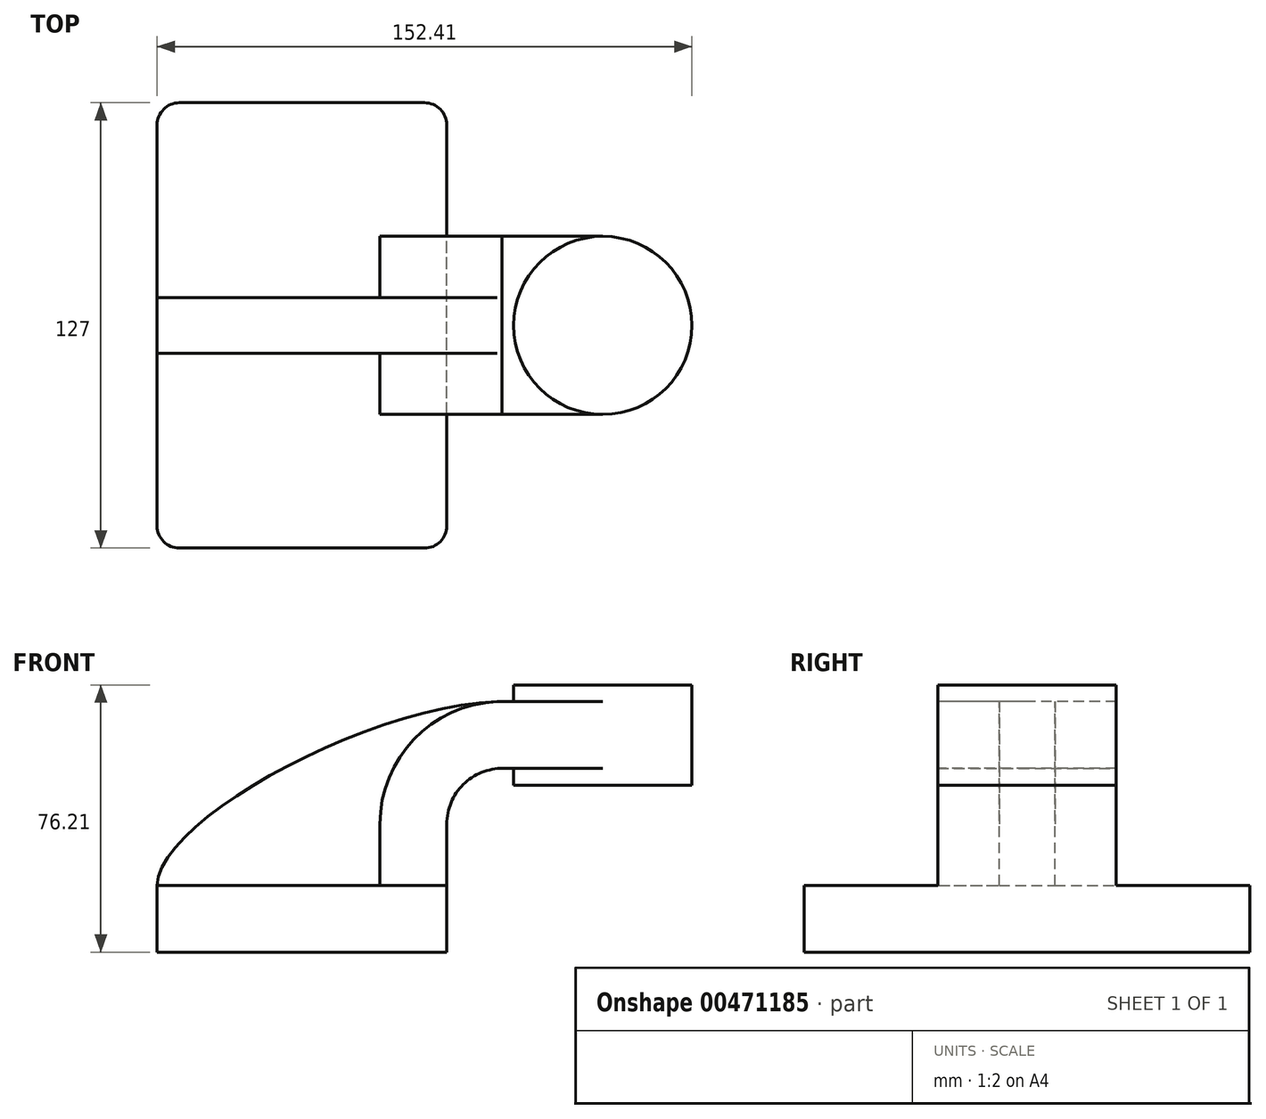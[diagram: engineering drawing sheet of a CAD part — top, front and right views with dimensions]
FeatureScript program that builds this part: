
annotation { "Feature Type Name" : "Feature", "Feature Type Description" : "" }
export const myFeature = defineFeature(function(context is Context, id is Id, definition is map)
    precondition{}
    {
        {
            var Q0;
            Q0=qCreatedBy(makeId("Front.planeOp"),FACE);
            var sketch = newSketch(context, id + "F0", { "sketchPlane" : qUnion([Q0])});
            skLineSegment(sketch, "E0.bottom", {"start": v(41.28, 9.53) * mm, "end": v(-41.28, 9.53) * mm});
            skLineSegment(sketch, "E0.top", {"start": v(41.28, -9.52) * mm, "end": v(-41.28, -9.52) * mm});
            skLineSegment(sketch, "E0.left", {"start": v(41.28, 9.53) * mm, "end": v(41.28, -9.52) * mm});
            skLineSegment(sketch, "E0.right", {"start": v(-41.28, 9.53) * mm, "end": v(-41.28, -9.52) * mm});
            skPoint(sketch, "E0.middle", {"position": v(0, 0) * mm});
            skLineSegment(sketch, "E1.bottom", {"start": v(111.13, 38.1) * mm, "end": v(60.33, 38.1) * mm});
            skLineSegment(sketch, "E1.top", {"start": v(111.13, 66.68) * mm, "end": v(60.33, 66.68) * mm});
            skLineSegment(sketch, "E1.left", {"start": v(111.13, 38.1) * mm, "end": v(111.13, 66.68) * mm});
            skLineSegment(sketch, "E1.right", {"start": v(60.33, 38.1) * mm, "end": v(60.33, 66.68) * mm});
            skPoint(sketch, "E1.middle", {"position": v(85.73, 52.39) * mm});
            skLineSegment(sketch, "E2", {"start": v(41.28, 9.53) * mm, "end": v(41.28, 27) * mm});
            skArc(sketch, "E3", {"start": v(41.28, 27) * mm, "mid": v(45.97, 38.27) * mm, "end": v(57.27, 42.88) * mm});
            skLineSegment(sketch, "E4", {"start": v(57.27, 42.88) * mm, "end": v(85.73, 42.88) * mm});
            skPoint(sketch, "E4.endSnap0", {"position": v(85.73, 38.1) * mm});
            skLineSegment(sketch, "E5.0", {"start": v(56.98, 61.93) * mm, "end": v(85.73, 61.93) * mm});
            skArc(sketch, "E5.1", {"start": v(22.23, 27) * mm, "mid": v(32.4, 51.64) * mm, "end": v(56.98, 61.93) * mm});
            skLineSegment(sketch, "E5.2", {"start": v(22.22, 9.53) * mm, "end": v(22.22, 27) * mm});
            skFitSpline(sketch, "E6", {"points": [v(-41.28, 9.52) * mm, v(56.98, 61.93) * mm], "startDerivative": vector(1.29, 56.57) * mm, "endDerivative": vector(111.42, 1.59) * mm});
            skLineSegment(sketch, "E7", {"start": v(85.73, 38.1) * mm, "end": v(85.73, 66.68) * mm});
            skSolve(sketch);
        }
        {
            var Q0;
            Q0=makeQuery(id+"F0.imprint","IMPRINT",FACE,{"disambiguationData":[TD([[makeQuery(id+"F0.imprint","IMPRINT",EDGE,{"derivedFrom":sQuery(id+"F0.wireOp",EDGE,"E0.top")}),-1.0]])]});
            var Q1;
            Q1=sQuery(id+"F0.wireOp",EDGE,"E6");
            extrude(context, id + "F1", {"entities" : qUnion([Q0]), "surfaceEntities" : qUnion([Q1]), "endBound" : BoundingType.SYMMETRIC, "depth" : 127 * mm});
        }
        {
            var Q0;
            {var subQ1=sQuery(id+"F0.wireOp",EDGE,"E2");Q0=makeQuery(id+"F0.imprint","IMPRINT",FACE,{"disambiguationData":[TD([[makeQuery(id+"F0.imprint","IMPRINT",EDGE,{"derivedFrom":subQ1}),1.0]])]});}
            var Q1;
            {var subQ5=sQuery(id+"F0.wireOp",EDGE,"w3ybBXN1-ukuw-oLe4-pjF5-DVVGLDHJmDPz");Q1=makeQuery(id+"F0.imprint","IMPRINT",FACE,{"disambiguationData":[TD([[makeQuery(id+"F0.imprint","IMPRINT",EDGE,{"derivedFrom":subQ5}),1.0]])]});}
            var Q2;
            {var subQ0=sQuery(id+"F0.wireOp",EDGE,"E4");var subQ1=sQuery(id+"F0.wireOp",EDGE,"E1.right");var subQ2=makeQuery(id+"F0.imprint","INTERSECT",VERTEX,{"derivedFrom":[subQ1,subQ0]});Q2=makeQuery(id+"F0.imprint","IMPRINT",FACE,{"disambiguationData":[TD([[makeQuery(id+"F0.imprint","IMPRINT",EDGE,{"disambiguationData":[TD([[subQ2,-1.0]])],"derivedFrom":subQ1}),-1.0]])]});}
            extrude(context, id + "F2", {"entities" : qUnion([Q0, Q1, Q2]), "operationType" : NewBodyOperationType.ADD, "endBound" : BoundingType.SYMMETRIC, "depth" : 50.8 * mm});
        }
        {
            var Q0;
            {var subQ3=sQuery(id+"F0.wireOp",EDGE,"E5.2");Q0=makeQuery(id+"F0.imprint","IMPRINT",FACE,{"disambiguationData":[TD([[makeQuery(id+"F0.imprint","IMPRINT",EDGE,{"derivedFrom":subQ3}),1.0]])]});}
            extrude(context, id + "F3", {"entities" : qUnion([Q0]), "operationType" : NewBodyOperationType.ADD, "endBound" : BoundingType.SYMMETRIC, "depth" : 15.88 * mm});
        }
        {
            var Q0;
            {var subQ4=sQuery(id+"F0.wireOp",EDGE,"E1.left");Q0=makeQuery(id+"F0.imprint","IMPRINT",FACE,{"disambiguationData":[TD([[makeQuery(id+"F0.imprint","IMPRINT",EDGE,{"derivedFrom":subQ4}),1.0]])]});}
            var Q1;
            Q1=sQuery(id+"F0.wireOp",EDGE,"E7");
            revolve(context, id + "F4", {"operationType" : NewBodyOperationType.ADD, "entities" : qUnion([Q0]), "axis" : qUnion([Q1]), "revolveType" : RevolveType.FULL});
        }
        {
            var Q0;
            Q0=makeQuery(id+"F1.opExtrude","CAP_EDGE",EDGE,{"disambiguationData":[OSD([sQuery(id+"F0.wireOp",EDGE,"E0.right")])],"isStart":false});
            var Q1;
            Q1=makeQuery(id+"F1.opExtrude","CAP_EDGE",EDGE,{"disambiguationData":[OSD([sQuery(id+"F0.wireOp",EDGE,"E0.left")])],"isStart":false});
            var Q2;
            Q2=makeQuery(id+"F1.opExtrude","CAP_EDGE",EDGE,{"disambiguationData":[OSD([sQuery(id+"F0.wireOp",EDGE,"E0.left")])],"isStart":true});
            var Q3;
            Q3=makeQuery(id+"F1.opExtrude","CAP_EDGE",EDGE,{"disambiguationData":[OSD([sQuery(id+"F0.wireOp",EDGE,"E0.right")])],"isStart":true});
            fillet(context, id + "F5", {"entities" : qUnion([Q0, Q1, Q2, Q3]), "radius" : 6.35 * mm, "tangentPropagation" : true, "allowEdgeOverflow" : false});
        }
    });
